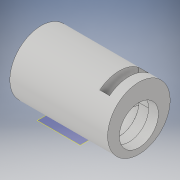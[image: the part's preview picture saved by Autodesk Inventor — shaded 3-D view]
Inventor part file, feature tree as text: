
AUTODESK INVENTOR PART (.ipt)
format: ipt  version: 2019 (Build 230136000, 136)  size: 268,800 bytes
history: native  units: in
note: dims shown in document units (in); Inventor stores cm internally (conversion verified against a paired STEP export)
features: sketch x9, extrude x4, revolve x1, loft x1, fillet x1, plane x1, other x1
ambient origin geometry x8: Origin, YZ Plane, XZ Plane, XY Plane, X Axis, Y Axis, Z Axis, Center Point
bodies: Solid1 (feature_tree)
feature tree (18):
  revolve  "Revolution1"  [1 undecoded]
  sketch  "Sketch2"  dims[d3=0.7874in d4=90.0deg]
  extrude  "Extrusion1"  TaperAngle=90.0deg  [1 undecoded]
  sketch  "Sketch4"  dims[d9=0.7874in d10=0.0in d11=90.0deg]
  sketch  "Sketch5"  dims[d12=0.0in d13=90.0deg d14=0.2362in]
  loft  "Loft1"
  fillet  "Fillet1"  Radius=0.3937in
  sketch  "Sketch6"  dims[d15=0.5118in d16=0.1969in d17=0.0in]
  plane  "Work Plane1"
  extrude  "Extrusion2"  TaperAngle=0.0deg  [1 undecoded]
  extrude  "Extrusion3"  Depth=0.2362in
  extrude  "Extrusion4"  Depth=0.1969in TaperAngle=0.0deg
  sketch  "Sketch1"  dims[d0=0.1181in d1=0.7874in]
  sketch  "Sketch3"  dims[d5=0.0591in d6=0.5118in d7=0.3937in d8=0.0in]
  other  "Edges1"
  sketch  "Sketch7"  dims[d18=0.6299in]
  sketch  "Sketch8"  dims[d19=0.7177in]
  sketch  "Sketch9"  dims[d22=0.3937in d24=0.1969in d25=0.0in d26=1.2598in d28=0.3937in d29=0.1199in d30=0.1969in d31=0.0in]
note: 3 required parameter values undecoded (feature->parameter linkage not recoverable at this tier; creation-order binding heuristic only, values carry confidence <= 0.55)